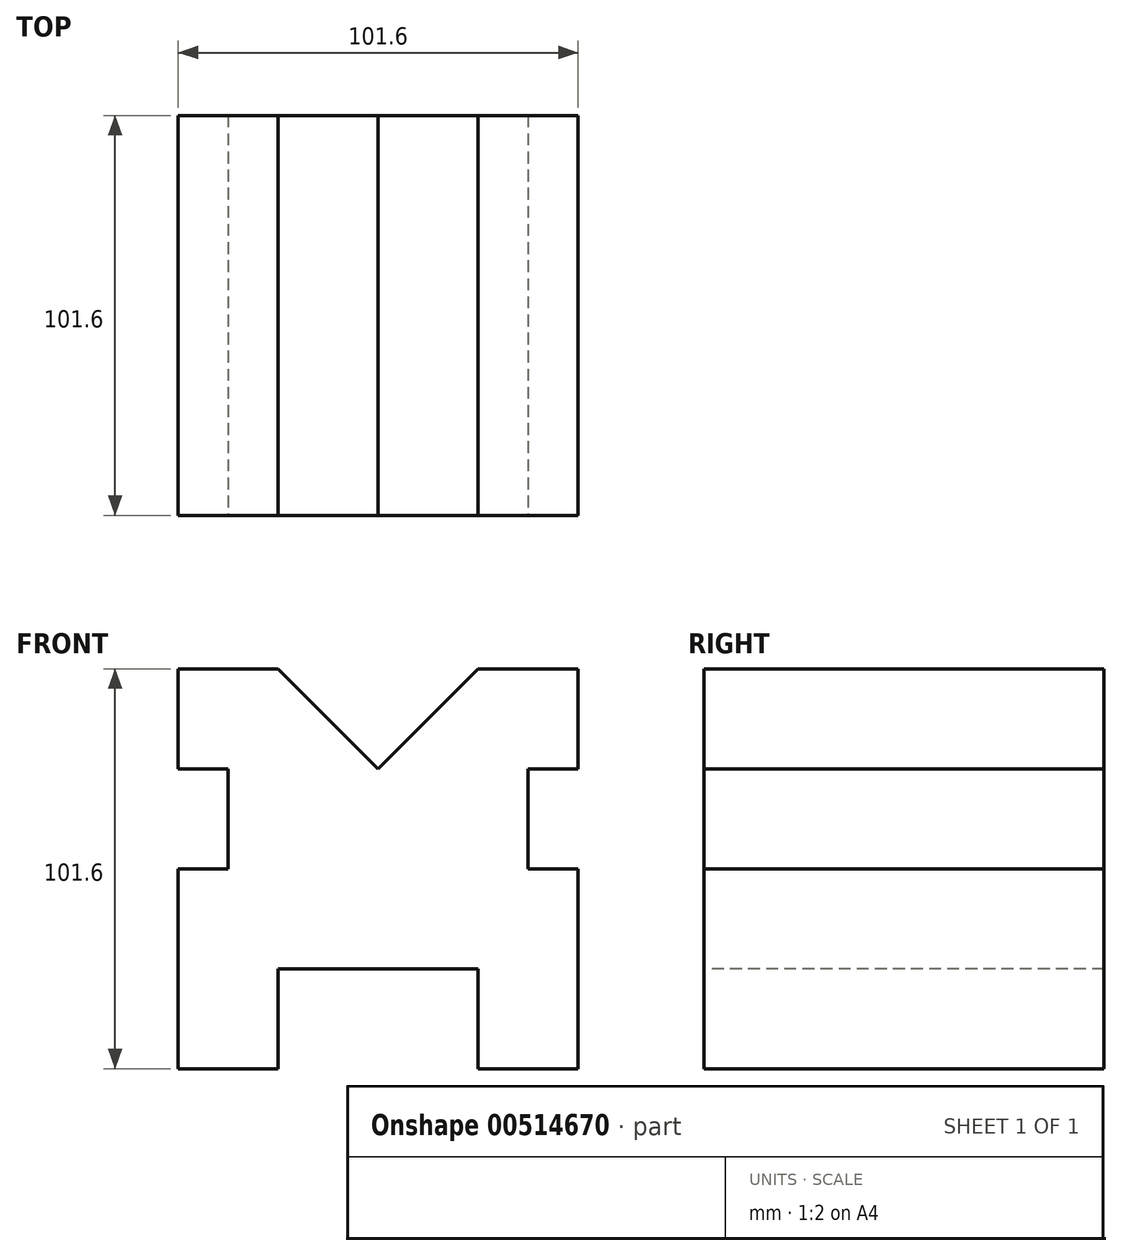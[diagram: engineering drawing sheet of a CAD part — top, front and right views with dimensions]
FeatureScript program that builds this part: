
annotation { "Feature Type Name" : "Feature", "Feature Type Description" : "" }
export const myFeature = defineFeature(function(context is Context, id is Id, definition is map)
    precondition{}
    {
        {
            var Q0;
            Q0=qCreatedBy(makeId("Top.planeOp"),FACE);
            var sketch = newSketch(context, id + "F0", { "sketchPlane" : qUnion([Q0])});
            skLineSegment(sketch, "E0.bottom", {"start": v(0, 0) * mm, "end": v(-101.6, 0) * mm});
            skLineSegment(sketch, "E0.top", {"start": v(0, -101.6) * mm, "end": v(-101.6, -101.6) * mm});
            skLineSegment(sketch, "E0.left", {"start": v(0, 0) * mm, "end": v(0, -101.6) * mm});
            skLineSegment(sketch, "E0.right", {"start": v(-101.6, 0) * mm, "end": v(-101.6, -101.6) * mm});
            skSolve(sketch);
        }
        {
            var Q0;
            Q0=makeQuery(id+"F0.imprint","IMPRINT",FACE,{"disambiguationData":[TD([[makeQuery(id+"F0.imprint","IMPRINT",EDGE,{"derivedFrom":sQuery(id+"F0.wireOp",EDGE,"E0.bottom")}),1.0]])]});
            extrude(context, id + "F1", {"entities" : qUnion([Q0]), "depth" : 101.6 * mm, "offsetDistance" : 25.4 * mm});
        }
        {
            var Q0;
            Q0=makeQuery(id+"F1.opExtrude","SWEPT_FACE",FACE,{"disambiguationData":[OSD([sQuery(id+"F0.wireOp",EDGE,"E0.top")])]});
            var sketch = newSketch(context, id + "F2", { "sketchPlane" : qUnion([Q0])});
            skLineSegment(sketch, "E1.bottom", {"start": v(-101.6, 101.6) * mm, "end": v(-76.2, 101.6) * mm});
            skLineSegment(sketch, "E1.top", {"start": v(-101.6, 0) * mm, "end": v(-76.2, 0) * mm});
            skLineSegment(sketch, "E1.left", {"start": v(-101.6, 101.6) * mm, "end": v(-101.6, 0) * mm});
            skLineSegment(sketch, "E1.right", {"start": v(-76.2, 101.6) * mm, "end": v(-76.2, 0) * mm});
            skLineSegment(sketch, "E2.bottom", {"start": v(0, 101.6) * mm, "end": v(-25.4, 101.6) * mm});
            skLineSegment(sketch, "E2.top", {"start": v(0, 0) * mm, "end": v(-25.4, 0) * mm});
            skLineSegment(sketch, "E2.left", {"start": v(0, 101.6) * mm, "end": v(0, 0) * mm});
            skLineSegment(sketch, "E2.right", {"start": v(-25.4, 101.6) * mm, "end": v(-25.4, 0) * mm});
            skLineSegment(sketch, "E3.bottom", {"start": v(-101.6, 101.6) * mm, "end": v(0, 101.6) * mm});
            skLineSegment(sketch, "E3.top", {"start": v(-101.6, 76.2) * mm, "end": v(0, 76.2) * mm});
            skLineSegment(sketch, "E3.left", {"start": v(-101.6, 101.6) * mm, "end": v(-101.6, 76.2) * mm});
            skLineSegment(sketch, "E3.right", {"start": v(0, 101.6) * mm, "end": v(0, 76.2) * mm});
            skLineSegment(sketch, "E4.bottom", {"start": v(-101.6, 101.6) * mm, "end": v(-50.8, 101.6) * mm});
            skLineSegment(sketch, "E4.top", {"start": v(-101.6, 0) * mm, "end": v(-50.8, 0) * mm});
            skLineSegment(sketch, "E4.right", {"start": v(-50.8, 101.6) * mm, "end": v(-50.8, 0) * mm});
            skLineSegment(sketch, "E5", {"start": v(-76.2, 101.6) * mm, "end": v(-50.8, 76.2) * mm});
            skLineSegment(sketch, "E6", {"start": v(-50.8, 76.2) * mm, "end": v(-25.4, 101.6) * mm});
            skSolve(sketch);
        }
        {
            var Q0;
            {var subQ0=sQuery(id+"F2.wireOp",EDGE,"E5");Q0=makeQuery(id+"F2.imprint","IMPRINT",FACE,{"disambiguationData":[TD([[makeQuery(id+"F2.imprint","IMPRINT",EDGE,{"derivedFrom":subQ0}),1.0]])]});}
            var Q1;
            {var subQ0=sQuery(id+"F2.wireOp",EDGE,"E6");Q1=makeQuery(id+"F2.imprint","IMPRINT",FACE,{"disambiguationData":[TD([[makeQuery(id+"F2.imprint","IMPRINT",EDGE,{"derivedFrom":subQ0}),1.0]])]});}
            extrude(context, id + "F3", {"entities" : qUnion([Q0, Q1]), "operationType" : NewBodyOperationType.REMOVE, "oppositeDirection" : true, "depth" : 132.08 * mm, "offsetDistance" : 25.4 * mm});
        }
        {
            var Q0;
            Q0=makeQuery(id+"F1.opExtrude","SWEPT_FACE",FACE,{"disambiguationData":[OSD([sQuery(id+"F0.wireOp",EDGE,"E0.top")])]});
            var sketch = newSketch(context, id + "F4", { "sketchPlane" : qUnion([Q0])});
            skLineSegment(sketch, "E7", {"start": v(-101.6, 101.6) * mm, "end": v(-101.6, 76.2) * mm});
            skLineSegment(sketch, "E8", {"start": v(-101.6, 76.2) * mm, "end": v(-88.9, 76.2) * mm});
            skLineSegment(sketch, "E9", {"start": v(-88.9, 76.2) * mm, "end": v(-88.9, 50.8) * mm});
            skLineSegment(sketch, "E10", {"start": v(-88.9, 50.8) * mm, "end": v(-101.6, 50.8) * mm});
            skLineSegment(sketch, "E11", {"start": v(0, 101.6) * mm, "end": v(0, 76.2) * mm});
            skLineSegment(sketch, "E12", {"start": v(0, 76.2) * mm, "end": v(-12.7, 76.2) * mm});
            skLineSegment(sketch, "E13", {"start": v(-12.7, 76.2) * mm, "end": v(-12.7, 50.8) * mm});
            skLineSegment(sketch, "E14", {"start": v(-12.7, 50.8) * mm, "end": v(2.36, 50.8) * mm});
            skPoint(sketch, "E14.endSnap0", {"position": v(0, 50.8) * mm});
            skSolve(sketch);
        }
        {
            var Q0;
            {var subQ0=sQuery(id+"F4.wireOp",EDGE,"E12");Q0=makeQuery(id+"F4.imprint","IMPRINT",FACE,{"disambiguationData":[TD([[makeQuery(id+"F4.imprint","IMPRINT",EDGE,{"derivedFrom":subQ0}),1.0]])]});}
            var Q1;
            {var subQ0=sQuery(id+"F4.wireOp",EDGE,"E8");Q1=makeQuery(id+"F4.imprint","IMPRINT",FACE,{"disambiguationData":[TD([[makeQuery(id+"F4.imprint","IMPRINT",EDGE,{"derivedFrom":subQ0}),-1.0]])]});}
            extrude(context, id + "F5", {"entities" : qUnion([Q0, Q1]), "operationType" : NewBodyOperationType.REMOVE, "oppositeDirection" : true, "depth" : 174.24 * mm, "offsetDistance" : 25.4 * mm});
        }
        {
            var Q0;
            Q0=makeQuery(id+"F1.opExtrude","SWEPT_FACE",FACE,{"disambiguationData":[OSD([sQuery(id+"F0.wireOp",EDGE,"E0.top")])]});
            var sketch = newSketch(context, id + "F6", { "sketchPlane" : qUnion([Q0])});
            skLineSegment(sketch, "E15", {"start": v(-101.6, 0) * mm, "end": v(-76.2, 0) * mm});
            skLineSegment(sketch, "E16", {"start": v(-76.2, 0) * mm, "end": v(-76.2, 25.4) * mm});
            skLineSegment(sketch, "E17", {"start": v(-76.2, 25.4) * mm, "end": v(-25.4, 25.4) * mm});
            skLineSegment(sketch, "E18", {"start": v(-25.4, 25.4) * mm, "end": v(-25.4, 0) * mm});
            skSolve(sketch);
        }
        {
            var Q0;
            {var subQ0=sQuery(id+"F6.wireOp",EDGE,"E16");Q0=makeQuery(id+"F6.imprint","IMPRINT",FACE,{"disambiguationData":[TD([[makeQuery(id+"F6.imprint","IMPRINT",EDGE,{"derivedFrom":subQ0}),-1.0]])]});}
            extrude(context, id + "F7", {"entities" : qUnion([Q0]), "operationType" : NewBodyOperationType.REMOVE, "oppositeDirection" : true, "depth" : 294.64 * mm, "offsetDistance" : 25.4 * mm});
        }
    });
